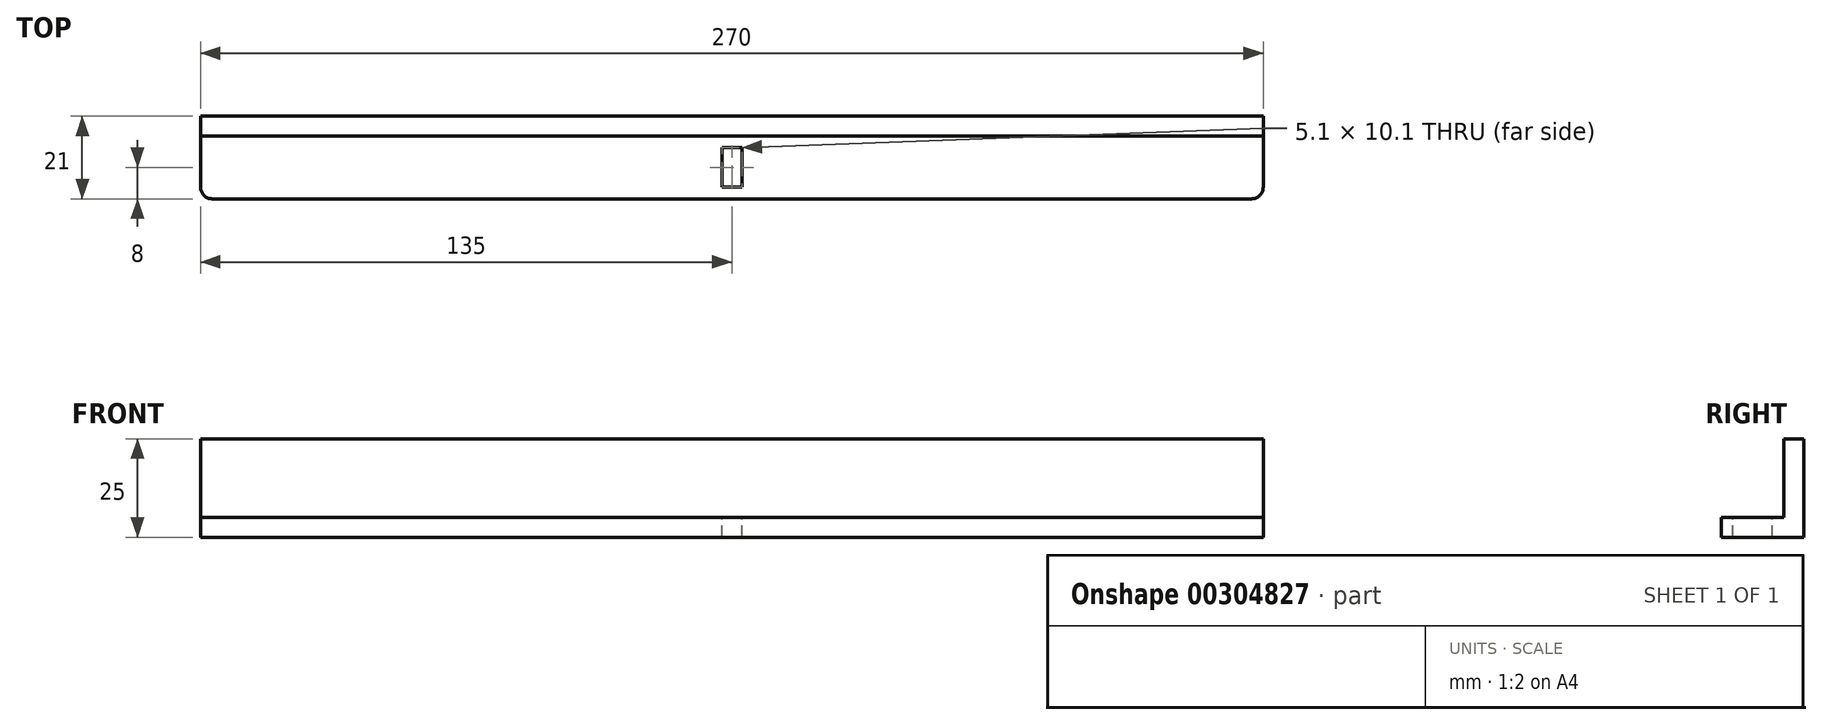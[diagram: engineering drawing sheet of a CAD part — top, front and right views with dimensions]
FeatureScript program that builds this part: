
annotation { "Feature Type Name" : "Feature", "Feature Type Description" : "" }
export const myFeature = defineFeature(function(context is Context, id is Id, definition is map)
    precondition{}
    {
        {
            var Q0;
            Q0=qCreatedBy(makeId("Top.planeOp"),FACE);
            var sketch = newSketch(context, id + "F0", { "sketchPlane" : qUnion([Q0])});
            skPoint(sketch, "E0", {"position": v(-70, 0) * mm});
            skPoint(sketch, "E1", {"position": v(0, 0) * mm});
            skLineSegment(sketch, "E2.bottom", {"start": v(-132, -8) * mm, "end": v(132, -8) * mm});
            skPoint(sketch, "E3", {"position": v(70, 0) * mm});
            skPoint(sketch, "E4", {"position": v(125, 0) * mm});
            skPoint(sketch, "E5", {"position": v(-125, 0) * mm});
            skLineSegment(sketch, "E6", {"start": v(-135, 13) * mm, "end": v(-135, -5) * mm});
            skLineSegment(sketch, "E7", {"start": v(-135, 13) * mm, "end": v(135, 13) * mm});
            skLineSegment(sketch, "E8.top", {"start": v(-135, 8) * mm, "end": v(135, 8) * mm});
            skLineSegment(sketch, "E8.left", {"start": v(-135, 13) * mm, "end": v(-135, 8) * mm});
            skLineSegment(sketch, "E9.bottom", {"start": v(2.55, -5.05) * mm, "end": v(-2.55, -5.05) * mm});
            skLineSegment(sketch, "E9.top", {"start": v(2.55, 5.05) * mm, "end": v(-2.55, 5.05) * mm});
            skLineSegment(sketch, "E9.left", {"start": v(2.55, -5.05) * mm, "end": v(2.55, 5.05) * mm});
            skLineSegment(sketch, "E9.right", {"start": v(-2.55, -5.05) * mm, "end": v(-2.55, 5.05) * mm});
            skPoint(sketch, "E10.visualSharp", {"position": v(-135, -8) * mm});
            skArc(sketch, "E10.filletArc", {"start": v(-135, -5) * mm, "mid": v(-134.12, -7.12) * mm, "end": v(-132, -8) * mm});
            skLineSegment(sketch, "E11", {"start": v(135, 13) * mm, "end": v(135, -5) * mm});
            skPoint(sketch, "E12.visualSharp", {"position": v(135, -8) * mm});
            skArc(sketch, "E12.filletArc", {"start": v(132, -8) * mm, "mid": v(134.12, -7.12) * mm, "end": v(135, -5) * mm});
            skSolve(sketch);
        }
        {
            var Q0;
            Q0=makeQuery(id+"F0.imprint","IMPRINT",FACE,{"disambiguationData":[TD([[makeQuery(id+"F0.imprint","IMPRINT",EDGE,{"derivedFrom":sQuery(id+"F0.wireOp",EDGE,"E7")}),-1.0]])]});
            extrude(context, id + "F1", {"entities" : qUnion([Q0]), "depth" : 20 * mm});
        }
        {
            var Q0;
            Q0=qSketchRegion(id+"F0",true);
            extrude(context, id + "F2", {"entities" : qUnion([Q0]), "operationType" : NewBodyOperationType.ADD, "oppositeDirection" : true, "depth" : 5 * mm});
        }
    });
